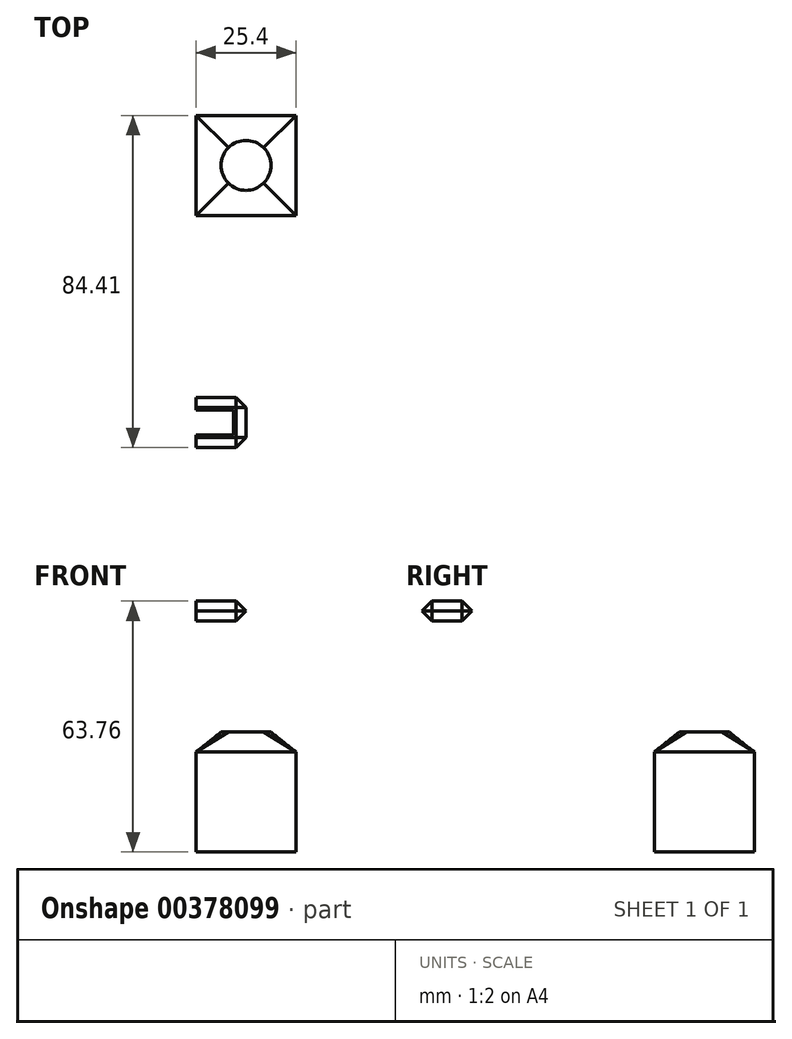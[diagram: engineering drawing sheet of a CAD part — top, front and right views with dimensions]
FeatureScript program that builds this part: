
annotation { "Feature Type Name" : "Feature", "Feature Type Description" : "" }
export const myFeature = defineFeature(function(context is Context, id is Id, definition is map)
    precondition{}
    {
        {
            var Q0;
            Q0=qCreatedBy(makeId("Top.planeOp"),FACE);
            var sketch = newSketch(context, id + "F0", { "sketchPlane" : qUnion([Q0])});
            skLineSegment(sketch, "E0.bottom", {"start": v(0, 0) * mm, "end": v(25.4, 0) * mm});
            skLineSegment(sketch, "E0.top", {"start": v(0, 25.4) * mm, "end": v(25.4, 25.4) * mm});
            skLineSegment(sketch, "E0.left", {"start": v(0, 0) * mm, "end": v(0, 25.4) * mm});
            skLineSegment(sketch, "E0.right", {"start": v(25.4, 0) * mm, "end": v(25.4, 25.4) * mm});
            skSolve(sketch);
        }
        {
            var Q0;
            Q0 = qSketchRegion(id + "F0", true);
            extrude(context, id + "F1", {"entities" : qUnion([Q0]), "depth" : 25.4 * mm});
        }
        {
            var Q0;
            Q0=makeQuery(id+"F1.opExtrude","CAP_FACE",FACE,{"disambiguationData":[OSD([sQuery(id+"F0.wireOp",EDGE,"E0.bottom"),sQuery(id+"F0.wireOp",EDGE,"E0.top"),sQuery(id+"F0.wireOp",EDGE,"E0.left"),sQuery(id+"F0.wireOp",EDGE,"E0.right")])],"isStart":false});
            cPlane(context, id + "F2", {"entities" : qUnion([Q0]), "cplaneType" : CPlaneType.OFFSET, "offset" : 5.08 * mm, "width" : 152.4 * mm, "height" : 152.4 * mm});
        }
        {
            var Q0;
            Q0=qCreatedBy(id+"F2.planeOp",FACE);
            var sketch = newSketch(context, id + "F3", { "sketchPlane" : qUnion([Q0])});
            skLineSegment(sketch, "E1", {"start": v(25.4, 0) * mm, "end": v(0, 0) * mm});
            skCircle(sketch, "E2", {"center": v(12.7, 12.7) * mm, "radius": 6.35 * mm});
            skPoint(sketch, "E3.end.orphan", {"position": v(25.4, 25.4) * mm});
            skSolve(sketch);
        }
        {
            var Q1;
            Q1=makeQuery(id+"F1.opExtrude","CAP_FACE",FACE,{"disambiguationData":[OSD([sQuery(id+"F0.wireOp",EDGE,"E0.bottom"),sQuery(id+"F0.wireOp",EDGE,"E0.top"),sQuery(id+"F0.wireOp",EDGE,"E0.left"),sQuery(id+"F0.wireOp",EDGE,"E0.right")])],"isStart":false});
            var Q2;
            Q2=makeQuery(id+"F3.imprint","IMPRINT",FACE,{"disambiguationData":[TD([[makeQuery(id+"F3.imprint","IMPRINT",EDGE,{"derivedFrom":sQuery(id+"F3.wireOp",EDGE,"E2")}),1.0]])]});
            loft(context, id + "F4", {"operationType" : NewBodyOperationType.ADD, "sheetProfilesArray" : [{ "sheetProfileEntities" : qUnion([Q1]) }, { "sheetProfileEntities" : qUnion([Q2]) }]});
        }
        {
            var Q0;
            Q0=makeQuery(id+"F1.opExtrude","SWEPT_BODY",BODY,{"disambiguationData":[OSD([sQuery(id+"F0.wireOp",EDGE,"E0.bottom"),sQuery(id+"F0.wireOp",EDGE,"E0.top"),sQuery(id+"F0.wireOp",EDGE,"E0.left"),sQuery(id+"F0.wireOp",EDGE,"E0.right")])]});
            transform(context, id + "F5", {"entities" : qUnion([Q0]), "transformType" : TransformType.TRANSLATION_3D, "dx" : 0 * mm, "dy" : 0 * mm, "dz" : 0 * mm, "makeCopy" : true});
        }
        {
            var Q0;
            Q0=makeQuery(id+"F5.opPattern","COPY",BODY,{"derivedFrom":makeQuery(id+"F1.opExtrude","SWEPT_BODY",BODY,{"disambiguationData":[OSD([sQuery(id+"F0.wireOp",EDGE,"E0.bottom"),sQuery(id+"F0.wireOp",EDGE,"E0.top"),sQuery(id+"F0.wireOp",EDGE,"E0.left"),sQuery(id+"F0.wireOp",EDGE,"E0.right")])]}),"instanceName":"1"});
            transform(context, id + "F6", {"entities" : qUnion([Q0]), "transformType" : TransformType.TRANSLATION_3D, "dx" : 0 * mm, "dy" : 0 * mm, "dz" : 0 * mm, "makeCopy" : true});
        }
        {
            var Q0;
            Q0=makeQuery(id+"F6.opPattern","COPY",BODY,{"derivedFrom":makeQuery(id+"F5.opPattern","COPY",BODY,{"derivedFrom":makeQuery(id+"F1.opExtrude","SWEPT_BODY",BODY,{"disambiguationData":[OSD([sQuery(id+"F0.wireOp",EDGE,"E0.bottom"),sQuery(id+"F0.wireOp",EDGE,"E0.top"),sQuery(id+"F0.wireOp",EDGE,"E0.left"),sQuery(id+"F0.wireOp",EDGE,"E0.right")])]}),"instanceName":"1"}),"instanceName":"1"});
            transform(context, id + "F7", {"entities" : qUnion([Q0]), "transformType" : TransformType.TRANSLATION_3D, "dx" : 0 * mm, "dy" : 0 * mm, "dz" : 0 * mm, "makeCopy" : true});
        }
        {
            var Q0;
            Q0=makeQuery(id+"F7.opPattern","COPY",BODY,{"derivedFrom":makeQuery(id+"F6.opPattern","COPY",BODY,{"derivedFrom":makeQuery(id+"F5.opPattern","COPY",BODY,{"derivedFrom":makeQuery(id+"F1.opExtrude","SWEPT_BODY",BODY,{"disambiguationData":[OSD([sQuery(id+"F0.wireOp",EDGE,"E0.bottom"),sQuery(id+"F0.wireOp",EDGE,"E0.top"),sQuery(id+"F0.wireOp",EDGE,"E0.left"),sQuery(id+"F0.wireOp",EDGE,"E0.right")])]}),"instanceName":"1"}),"instanceName":"1"}),"instanceName":"1"});
            transform(context, id + "F8", {"entities" : qUnion([Q0]), "transformType" : TransformType.TRANSLATION_3D, "dx" : 0 * mm, "dy" : 0 * mm, "dz" : 0 * mm, "makeCopy" : true});
        }
        {
            var Q0;
            Q0=makeQuery(id+"F8.opPattern","COPY",BODY,{"derivedFrom":makeQuery(id+"F7.opPattern","COPY",BODY,{"derivedFrom":makeQuery(id+"F6.opPattern","COPY",BODY,{"derivedFrom":makeQuery(id+"F5.opPattern","COPY",BODY,{"derivedFrom":makeQuery(id+"F1.opExtrude","SWEPT_BODY",BODY,{"disambiguationData":[OSD([sQuery(id+"F0.wireOp",EDGE,"E0.bottom"),sQuery(id+"F0.wireOp",EDGE,"E0.top"),sQuery(id+"F0.wireOp",EDGE,"E0.left"),sQuery(id+"F0.wireOp",EDGE,"E0.right")])]}),"instanceName":"1"}),"instanceName":"1"}),"instanceName":"1"}),"instanceName":"1"});
            transform(context, id + "F9", {"entities" : qUnion([Q0]), "transformType" : TransformType.TRANSLATION_3D, "dx" : 0 * mm, "dy" : 0 * mm, "dz" : 0 * mm, "makeCopy" : true});
        }
        {
            var Q0;
            Q0=qCreatedBy(makeId("Right.planeOp"),FACE);
            var sketch = newSketch(context, id + "F10", { "sketchPlane" : qUnion([Q0])});
            skLineSegment(sketch, "E4.bottom", {"start": v(-59.01, 63.76) * mm, "end": v(-46.31, 63.76) * mm});
            skLineSegment(sketch, "E4.top", {"start": v(-59.01, 58.68) * mm, "end": v(-46.31, 58.68) * mm});
            skLineSegment(sketch, "E4.left", {"start": v(-59.01, 63.76) * mm, "end": v(-59.01, 58.68) * mm});
            skLineSegment(sketch, "E4.right", {"start": v(-46.31, 63.76) * mm, "end": v(-46.31, 58.68) * mm});
            skSolve(sketch);
        }
        {
            var Q0;
            Q0=makeQuery(id+"F10.imprint","IMPRINT",FACE,{"disambiguationData":[TD([[makeQuery(id+"F10.imprint","IMPRINT",EDGE,{"derivedFrom":sQuery(id+"F10.wireOp",EDGE,"E4.bottom")}),-1.0]])]});
            extrude(context, id + "F11", {"entities" : qUnion([Q0]), "depth" : 12.7 * mm});
        }
        {
            var Q0;
            Q0=makeQuery(id+"F11.opExtrude","SWEPT_FACE",FACE,{"disambiguationData":[OSD([sQuery(id+"F10.wireOp",EDGE,"E4.top")])]});
            var sketch = newSketch(context, id + "F12", { "sketchPlane" : qUnion([Q0])});
            skPoint(sketch, "E5.endSnap0", {"position": v(0, 52.66) * mm});
            skLineSegment(sketch, "E6", {"start": v(0, 59.01) * mm, "end": v(0, 52.66) * mm});
            skLineSegment(sketch, "E7", {"start": v(0, 55.84) * mm, "end": v(9.53, 55.84) * mm});
            skLineSegment(sketch, "E8", {"start": v(9.53, 55.84) * mm, "end": v(6.35, 55.84) * mm});
            skLineSegment(sketch, "E9", {"start": v(6.35, 59.01) * mm, "end": v(12.7, 59.01) * mm});
            skLineSegment(sketch, "E10", {"start": v(12.7, 59.01) * mm, "end": v(9.53, 59.01) * mm});
            skLineSegment(sketch, "E11", {"start": v(9.53, 55.84) * mm, "end": v(9.53, 49.49) * mm});
            skLineSegment(sketch, "E12", {"start": v(9.53, 46.31) * mm, "end": v(12.7, 46.31) * mm});
            skLineSegment(sketch, "E13", {"start": v(12.7, 46.31) * mm, "end": v(0, 46.31) * mm});
            skLineSegment(sketch, "E14", {"start": v(0, 46.31) * mm, "end": v(0, 52.66) * mm});
            skLineSegment(sketch, "E15", {"start": v(0, 49.49) * mm, "end": v(9.53, 49.49) * mm});
            skPoint(sketch, "E16.orphan", {"position": v(12.7, 55.84) * mm});
            skSolve(sketch);
        }
        {
            var Q0;
            {var subQ0=sQuery(id+"F12.wireOp",EDGE,"E7");Q0=makeQuery(id+"F12.imprint","IMPRINT",FACE,{"disambiguationData":[TD([[makeQuery(id+"F12.imprint","IMPRINT",EDGE,{"derivedFrom":subQ0}),-1.0]])]});}
            extrude(context, id + "F13", {"entities" : qUnion([Q0]), "operationType" : NewBodyOperationType.REMOVE, "oppositeDirection" : true, "depth" : 5.08 * mm});
        }
        {
            var Q0;
            Q0=makeQuery(id+"F11.opExtrude","CAP_EDGE",EDGE,{"disambiguationData":[OSD([sQuery(id+"F10.wireOp",EDGE,"E4.left")])],"isStart":false});
            var Q1;
            Q1=makeQuery(id+"F11.opExtrude","CAP_EDGE",EDGE,{"disambiguationData":[OSD([sQuery(id+"F10.wireOp",EDGE,"E4.right")])],"isStart":false});
            var Q2;
            Q2=makeQuery(id+"F11.opExtrude","CAP_EDGE",EDGE,{"disambiguationData":[OSD([sQuery(id+"F10.wireOp",EDGE,"E4.top")])],"isStart":false});
            var Q3;
            Q3=makeQuery(id+"F11.opExtrude","CAP_EDGE",EDGE,{"disambiguationData":[OSD([sQuery(id+"F10.wireOp",EDGE,"E4.bottom")])],"isStart":false});
            var Q4;
            Q4=makeQuery(id+"F11.opExtrude","SWEPT_EDGE",EDGE,{"disambiguationData":[OSD([sQuery(id+"F10.wireOp",EDGE,"E4.top"),sQuery(id+"F10.wireOp",EDGE,"E4.right")])]});
            var Q5;
            Q5=makeQuery(id+"F11.opExtrude","SWEPT_EDGE",EDGE,{"disambiguationData":[OSD([sQuery(id+"F10.wireOp",EDGE,"E4.top"),sQuery(id+"F10.wireOp",EDGE,"E4.left")])]});
            var Q6;
            Q6=makeQuery(id+"F11.opExtrude","SWEPT_EDGE",EDGE,{"disambiguationData":[OSD([sQuery(id+"F10.wireOp",EDGE,"E4.bottom"),sQuery(id+"F10.wireOp",EDGE,"E4.left")])]});
            var Q7;
            Q7=makeQuery(id+"F11.opExtrude","SWEPT_EDGE",EDGE,{"disambiguationData":[OSD([sQuery(id+"F10.wireOp",EDGE,"E4.bottom"),sQuery(id+"F10.wireOp",EDGE,"E4.right")])]});
            chamfer(context, id + "F14", {"entities" : qUnion([Q0, Q1, Q2, Q3, Q4, Q5, Q6, Q7]), "width" : 2.54 * mm, "tangentPropagation" : true});
        }
    });
